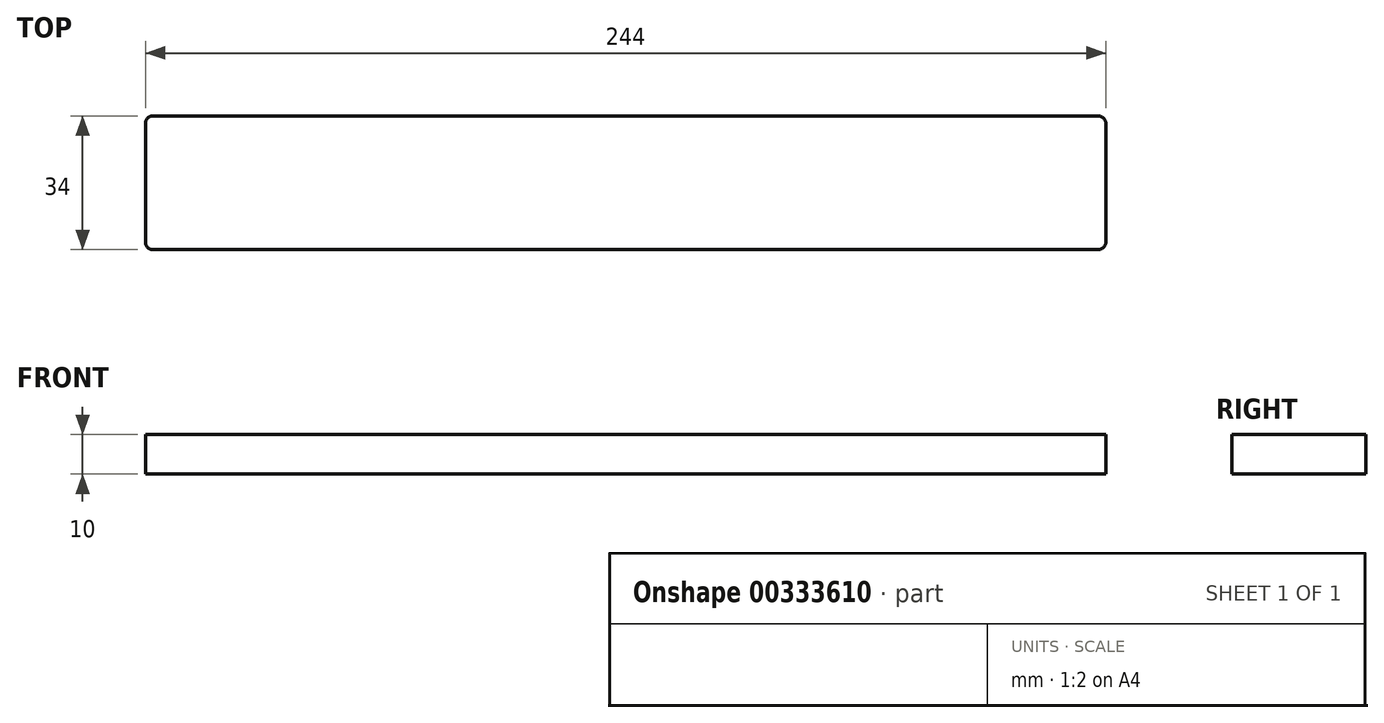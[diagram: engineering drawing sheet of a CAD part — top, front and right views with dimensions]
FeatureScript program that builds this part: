
annotation { "Feature Type Name" : "Feature", "Feature Type Description" : "" }
export const myFeature = defineFeature(function(context is Context, id is Id, definition is map)
    precondition{}
    {
        {
            var Q0;
            Q0=qCreatedBy(makeId("Top.planeOp"),FACE);
            var sketch = newSketch(context, id + "F0", { "sketchPlane" : qUnion([Q0])});
            skLineSegment(sketch, "E0.bottom", {"start": v(122, 17) * mm, "end": v(-122, 17) * mm});
            skLineSegment(sketch, "E0.top", {"start": v(122, -17) * mm, "end": v(-122, -17) * mm});
            skLineSegment(sketch, "E0.left", {"start": v(122, 17) * mm, "end": v(122, -17) * mm});
            skLineSegment(sketch, "E0.right", {"start": v(-122, 17) * mm, "end": v(-122, -17) * mm});
            skPoint(sketch, "E0.middle", {"position": v(0, 0) * mm});
            skSolve(sketch);
        }
        {
            var Q0;
            Q0=makeQuery(id+"F0.imprint","IMPRINT",FACE,{"disambiguationData":[TD([[makeQuery(id+"F0.imprint","IMPRINT",EDGE,{"derivedFrom":sQuery(id+"F0.wireOp",EDGE,"E0.bottom")}),1.0]])]});
            extrude(context, id + "F1", {"entities" : qUnion([Q0]), "depth" : 10 * mm});
        }
        {
            var Q0;
            Q0=makeQuery(id+"F1.opExtrude","SWEPT_EDGE",EDGE,{"disambiguationData":[OSD([sQuery(id+"F0.wireOp",EDGE,"E0.top"),sQuery(id+"F0.wireOp",EDGE,"E0.right")])]});
            var Q1;
            Q1=makeQuery(id+"F1.opExtrude","SWEPT_EDGE",EDGE,{"disambiguationData":[OSD([sQuery(id+"F0.wireOp",EDGE,"E0.bottom"),sQuery(id+"F0.wireOp",EDGE,"E0.right")])]});
            var Q2;
            Q2=makeQuery(id+"F1.opExtrude","SWEPT_EDGE",EDGE,{"disambiguationData":[OSD([sQuery(id+"F0.wireOp",EDGE,"E0.top"),sQuery(id+"F0.wireOp",EDGE,"E0.left")])]});
            var Q3;
            Q3=makeQuery(id+"F1.opExtrude","SWEPT_EDGE",EDGE,{"disambiguationData":[OSD([sQuery(id+"F0.wireOp",EDGE,"E0.bottom"),sQuery(id+"F0.wireOp",EDGE,"E0.left")])]});
            fillet(context, id + "F2", {"entities" : qUnion([Q0, Q1, Q2, Q3]), "radius" : 2 * mm, "tangentPropagation" : true, "allowEdgeOverflow" : false});
        }
    });
